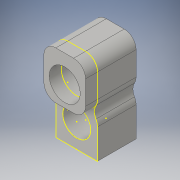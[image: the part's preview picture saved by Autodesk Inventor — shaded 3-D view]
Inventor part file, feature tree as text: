
AUTODESK INVENTOR PART (.ipt)
format: ipt  version: 2016 (Build 200138000, 138)  size: 185,344 bytes
history: native  units: mm
features: sketch x6, extrude x4, fillet x3, other x1, projected_geometry x1
ambient origin geometry x8: Origin, YZ Plane, XZ Plane, XY Plane, X Axis, Y Axis, Z Axis, Center Point
bodies: Body1 (feature_tree)
feature tree (15):
  other  "ソリッド1"
  extrude  "押し出し1"  Depth=7.0mm
  extrude  "押し出し2"  Depth=8.5mm
  fillet  "フィレット1"  Radius=15.0mm
  fillet  "フィレット2"  Radius=4.7mm
  sketch  "スケッチ4"
  extrude  "押し出し4"  Depth=4.0mm
  extrude  "押し出し5"  Depth=3.5mm
  fillet  "フィレット3"  Radius=5.2mm
  sketch  "スケッチ9"
  sketch  "スケッチ1"
  sketch  "スケッチ2"
  sketch  "スケッチ6"
  sketch  "スケッチ8"
  projected_geometry  "投影ループ1"
